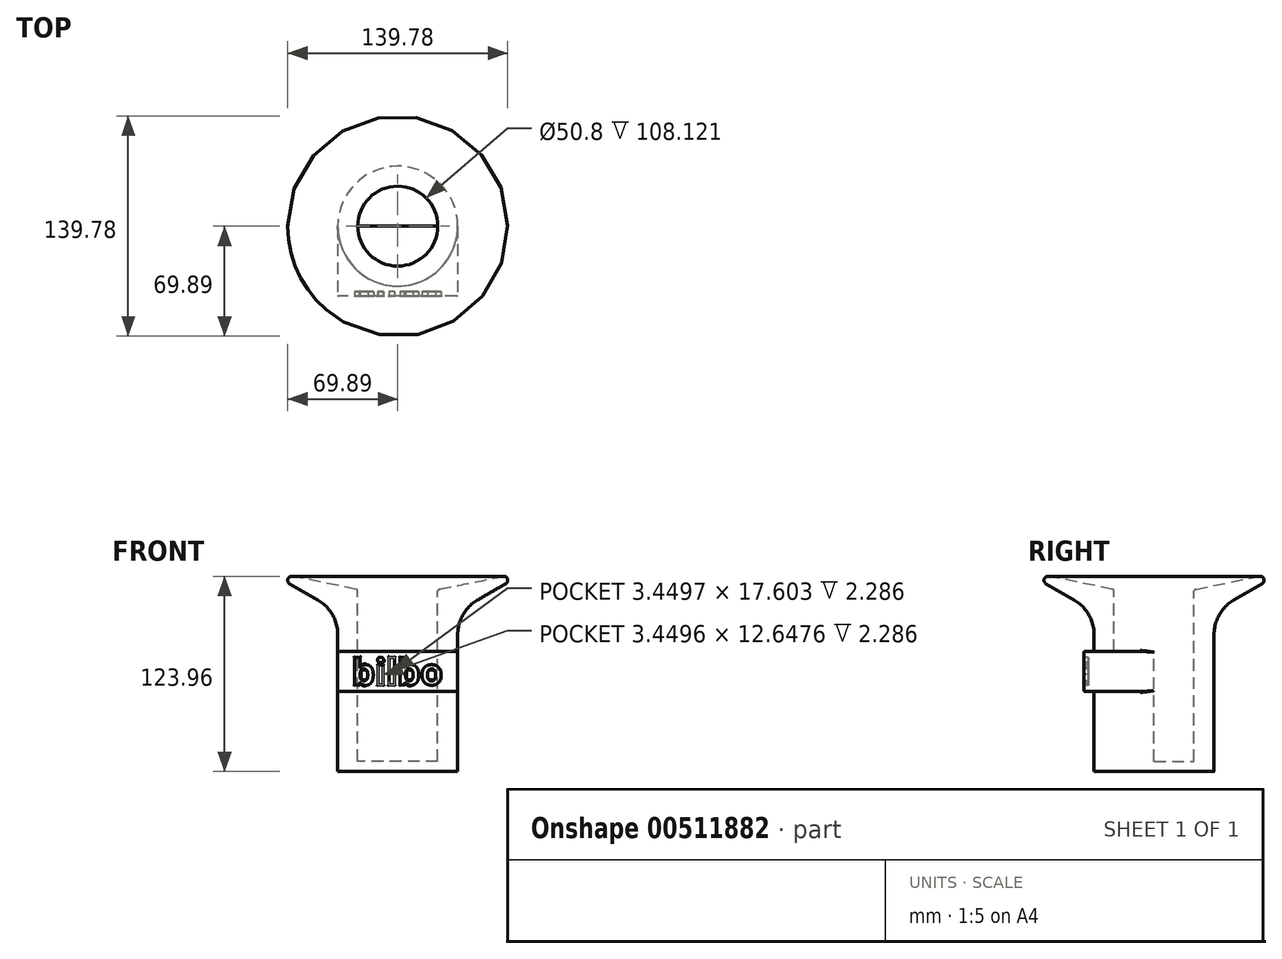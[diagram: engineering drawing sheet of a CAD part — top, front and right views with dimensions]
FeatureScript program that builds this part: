
annotation { "Feature Type Name" : "Feature", "Feature Type Description" : "" }
export const myFeature = defineFeature(function(context is Context, id is Id, definition is map)
    precondition{}
    {
        {
            var Q0;
            Q0=qCreatedBy(makeId("Front.planeOp"),FACE);
            var sketch = newSketch(context, id + "F0", { "sketchPlane" : qUnion([Q0])});
            skLineSegment(sketch, "E0", {"start": v(0, 0) * mm, "end": v(0, -6.35) * mm});
            skLineSegment(sketch, "E1", {"start": v(0, -6.35) * mm, "end": v(38.1, -6.35) * mm});
            skLineSegment(sketch, "E2", {"start": v(38.1, -6.35) * mm, "end": v(38.1, 95.25) * mm});
            skLineSegment(sketch, "E3", {"start": v(38.1, 95.25) * mm, "end": v(82.1, 120.65) * mm});
            skLineSegment(sketch, "E4", {"start": v(0, 0) * mm, "end": v(25.4, 0) * mm});
            skLineSegment(sketch, "E5", {"start": v(25.4, 0) * mm, "end": v(25.4, 109.16) * mm});
            skLineSegment(sketch, "E6", {"start": v(82.1, 120.65) * mm, "end": v(25.4, 109.16) * mm});
            skSolve(sketch);
        }
        {
            var Q0;
            Q0=makeQuery(id+"F0.imprint","IMPRINT",FACE,{"disambiguationData":[TD([[makeQuery(id+"F0.imprint","IMPRINT",EDGE,{"derivedFrom":sQuery(id+"F0.wireOp",EDGE,"E0")}),1.0]])]});
            var Q1;
            Q1=sQuery(id+"F0.wireOp",EDGE,"E0");
            revolve(context, id + "F1", {"entities" : qUnion([Q0]), "axis" : qUnion([Q1]), "revolveType" : RevolveType.FULL});
        }
        {
            var Q0;
            Q0=makeQuery(id+"F1.opRevolve","SWEPT_EDGE",EDGE,{"disambiguationData":[OSD([sQuery(id+"F0.wireOp",EDGE,"E3"),sQuery(id+"F0.wireOp",EDGE,"E6")])]});
            fillet(context, id + "F2", {"entities" : qUnion([Q0]), "radius" : 2.54 * mm, "tangentPropagation" : true, "allowEdgeOverflow" : false});
        }
        {
            var Q0;
            Q0=makeQuery(id+"F1.opRevolve","SWEPT_EDGE",EDGE,{"disambiguationData":[OSD([sQuery(id+"F0.wireOp",EDGE,"E5"),sQuery(id+"F0.wireOp",EDGE,"E6")])]});
            fillet(context, id + "F3", {"entities" : qUnion([Q0]), "radius" : 1.27 * mm, "tangentPropagation" : true, "allowEdgeOverflow" : false});
        }
        {
            var Q0;
            Q0=makeQuery(id+"F1.opRevolve","SWEPT_EDGE",EDGE,{"disambiguationData":[OSD([sQuery(id+"F0.wireOp",EDGE,"E2"),sQuery(id+"F0.wireOp",EDGE,"E3")])]});
            fillet(context, id + "F4", {"entities" : qUnion([Q0]), "radius" : 25.4 * mm, "tangentPropagation" : true, "allowEdgeOverflow" : false});
        }
        {
            var Q0;
            Q0=makeQuery(id+"F1.opRevolve","SWEPT_EDGE",EDGE,{"disambiguationData":[OSD([sQuery(id+"F0.wireOp",EDGE,"E1"),sQuery(id+"F0.wireOp",EDGE,"E2")])]});
            fillet(context, id + "F5", {"entities" : qUnion([Q0]), "radius" : 0.13 * mm, "tangentPropagation" : true, "allowEdgeOverflow" : false});
        }
        {
            var Q0;
            Q0=makeQuery(id+"F1.opRevolve","SWEPT_FACE",FACE,{"disambiguationData":[OSD([sQuery(id+"F0.wireOp",EDGE,"E1")])]});
            var sketch = newSketch(context, id + "F6", { "sketchPlane" : qUnion([Q0])});
            skLineSegment(sketch, "E7", {"start": v(0, 0) * mm, "end": v(-38.1, 0) * mm});
            skLineSegment(sketch, "E8", {"start": v(-38.1, 0) * mm, "end": v(38.1, 0) * mm});
            skLineSegment(sketch, "E9", {"start": v(0, 44.45) * mm, "end": v(-38.1, 44.45) * mm});
            skLineSegment(sketch, "E10", {"start": v(-38.1, 44.45) * mm, "end": v(38.1, 44.45) * mm});
            skLineSegment(sketch, "E11", {"start": v(38.1, 44.45) * mm, "end": v(38.1, 0) * mm});
            skLineSegment(sketch, "E12", {"start": v(-38.1, 44.45) * mm, "end": v(-38.1, 0) * mm});
            skSolve(sketch);
        }
        {
            var Q0;
            Q0=qSketchRegion(id+"F6",true);
            extrude(context, id + "F7", {"entities" : qUnion([Q0]), "operationType" : NewBodyOperationType.ADD, "depth" : -76.2 * mm});
        }
        {
            var Q0;
            Q0=makeQuery(id+"F7.boolean.opBoolean","MERGE",FACE,{"derivedFrom":[makeQuery(id+"F1.opRevolve","SWEPT_FACE",FACE,{"disambiguationData":[OSD([sQuery(id+"F0.wireOp",EDGE,"E1")])]}),makeQuery(id+"F7.opExtrude","CAP_FACE",FACE,{"disambiguationData":[OSD([sQuery(id+"F6.wireOp",EDGE,"E8"),sQuery(id+"F6.wireOp",EDGE,"E10"),sQuery(id+"F6.wireOp",EDGE,"E11"),sQuery(id+"F6.wireOp",EDGE,"E12")])],"isStart":true})]});
            var sketch = newSketch(context, id + "F8", { "sketchPlane" : qUnion([Q0])});
            skCircle(sketch, "E13", {"center": v(0, 0) * mm, "radius": 38.1 * mm});
            skCircle(sketch, "E14", {"center": v(0, 0) * mm, "radius": 62.93 * mm});
            skSolve(sketch);
        }
        {
            var Q0;
            Q0=makeQuery(id+"F8.imprint","IMPRINT",FACE,{"disambiguationData":[TD([[makeQuery(id+"F8.imprint","IMPRINT",EDGE,{"derivedFrom":sQuery(id+"F8.wireOp",EDGE,"E14")}),1.0]])]});
            var Q1;
            {var subQ3=sQuery(id+"F6.wireOp",EDGE,"E10");Q1=makeQuery(id+"F8.imprint","IMPRINT",FACE,{"disambiguationData":[TD([[makeQuery(id+"F8.imprint","IMPRINT",EDGE,{"derivedFrom":makeQuery(id+"F7.opExtrude","CAP_EDGE",EDGE,{"disambiguationData":[OSD([subQ3])],"isStart":true})}),-1.0]])]});}
            extrude(context, id + "F9", {"entities" : qUnion([Q0, Q1]), "operationType" : NewBodyOperationType.REMOVE, "oppositeDirection" : true, "depth" : 50.8 * mm});
        }
        {
            var Q0;
            Q0=makeQuery(id+"F7.opExtrude","SWEPT_FACE",FACE,{"disambiguationData":[OSD([sQuery(id+"F6.wireOp",EDGE,"E10")])]});
            var sketch = newSketch(context, id + "F10", { "sketchPlane" : qUnion([Q0])});
            skText(sketch, "E15", { "text": "bilbo\n", "fontName": "OpenSans-Bold.ttf"});
            skLineSegment(sketch, "E16.left", {"start": v(63.5, 69.85) * mm, "end": v(63.5, 44.45) * mm});
            skPoint(sketch, "E16.middle", {"position": v(0, 57.15) * mm});
            const initialGuessF10  = {"E15": [-0.0291, 0.04858, 1, 0, 0.01668]};
            skSetInitialGuess(sketch, initialGuessF10);
            skSolve(sketch);
        }
        {
            var Q0;
            Q0=qSketchRegion(id+"F10",true);
            extrude(context, id + "F11", {"entities" : qUnion([Q0]), "operationType" : NewBodyOperationType.REMOVE, "oppositeDirection" : true, "depth" : 2.8 * mm});
        }
        {
            var Q0;
            {var subQ1=sQuery(id+"F6.wireOp",EDGE,"E11");var subQ2=sQuery(id+"F6.wireOp",EDGE,"E10");Q0=makeQuery(id+"F11.boolean.opBoolean","SPLIT",FACE,{"disambiguationData":[TD([makeQuery(id+"F7.opExtrude","SWEPT_FACE",FACE,{"disambiguationData":[OSD([subQ1])]})])],"derivedFrom":makeQuery(id+"F7.opExtrude","SWEPT_FACE",FACE,{"disambiguationData":[OSD([subQ2])]})});}
            var Q1;
            Q1=makeQuery(id+"F11.boolean.opBoolean","SPLIT",FACE,{"disambiguationData":[TD([makeQuery(id+"F11.opExtrude","SWEPT_FACE",FACE,{"disambiguationData":[OSD([sQuery(id+"F10.wireOp",EDGE,"E15.sketch_text.stroke-14")])]})])],"derivedFrom":makeQuery(id+"F7.opExtrude","SWEPT_FACE",FACE,{"disambiguationData":[OSD([sQuery(id+"F6.wireOp",EDGE,"E10")])]})});
            var Q2;
            Q2=makeQuery(id+"F11.boolean.opBoolean","SPLIT",FACE,{"disambiguationData":[TD([makeQuery(id+"F11.opExtrude","SWEPT_FACE",FACE,{"disambiguationData":[OSD([sQuery(id+"F10.wireOp",EDGE,"E15.sketch_text.stroke-50")])]})])],"derivedFrom":makeQuery(id+"F7.opExtrude","SWEPT_FACE",FACE,{"disambiguationData":[OSD([sQuery(id+"F6.wireOp",EDGE,"E10")])]})});
            var Q3;
            Q3=makeQuery(id+"F11.boolean.opBoolean","SPLIT",FACE,{"disambiguationData":[TD([makeQuery(id+"F11.opExtrude","SWEPT_FACE",FACE,{"disambiguationData":[OSD([sQuery(id+"F10.wireOp",EDGE,"E15.sketch_text.stroke-59")])]})])],"derivedFrom":makeQuery(id+"F7.opExtrude","SWEPT_FACE",FACE,{"disambiguationData":[OSD([sQuery(id+"F6.wireOp",EDGE,"E10")])]})});
            fillet(context, id + "F12", {"entities" : qUnion([Q0, Q1, Q2, Q3]), "radius" : 0.5 * mm, "tangentPropagation" : true, "allowEdgeOverflow" : false});
        }
        {
            var Q0;
            Q0=makeQuery(id+"F7.opExtrude","SWEPT_FACE",FACE,{"disambiguationData":[OSD([sQuery(id+"F6.wireOp",EDGE,"E11")])]});
            var Q1;
            Q1=makeQuery(id+"F9.boolean.opBoolean","COPY",EDGE,{"derivedFrom":makeQuery(id+"F9.opExtrude","CAP_EDGE",EDGE,{"disambiguationData":[OSD([sQuery(id+"F8.wireOp",EDGE,"E13")])],"isStart":false})});
            var Q2;
            Q2=makeQuery(id+"F7.boolean.opBoolean","INTERSECT",EDGE,{"derivedFrom":[makeQuery(id+"F1.opRevolve","SWEPT_FACE",FACE,{"disambiguationData":[OSD([sQuery(id+"F0.wireOp",EDGE,"E2")])]}),makeQuery(id+"F7.opExtrude","CAP_FACE",FACE,{"disambiguationData":[OSD([sQuery(id+"F6.wireOp",EDGE,"E8"),sQuery(id+"F6.wireOp",EDGE,"E10"),sQuery(id+"F6.wireOp",EDGE,"E11"),sQuery(id+"F6.wireOp",EDGE,"E12")])],"isStart":false})]});
            var Q3;
            Q3=makeQuery(id+"F7.opExtrude","SWEPT_FACE",FACE,{"disambiguationData":[OSD([sQuery(id+"F6.wireOp",EDGE,"E12")])]});
            fillet(context, id + "F13", {"entities" : qUnion([Q0, Q1, Q2, Q3]), "radius" : 0.5 * mm, "tangentPropagation" : true, "allowEdgeOverflow" : false});
        }
    });
